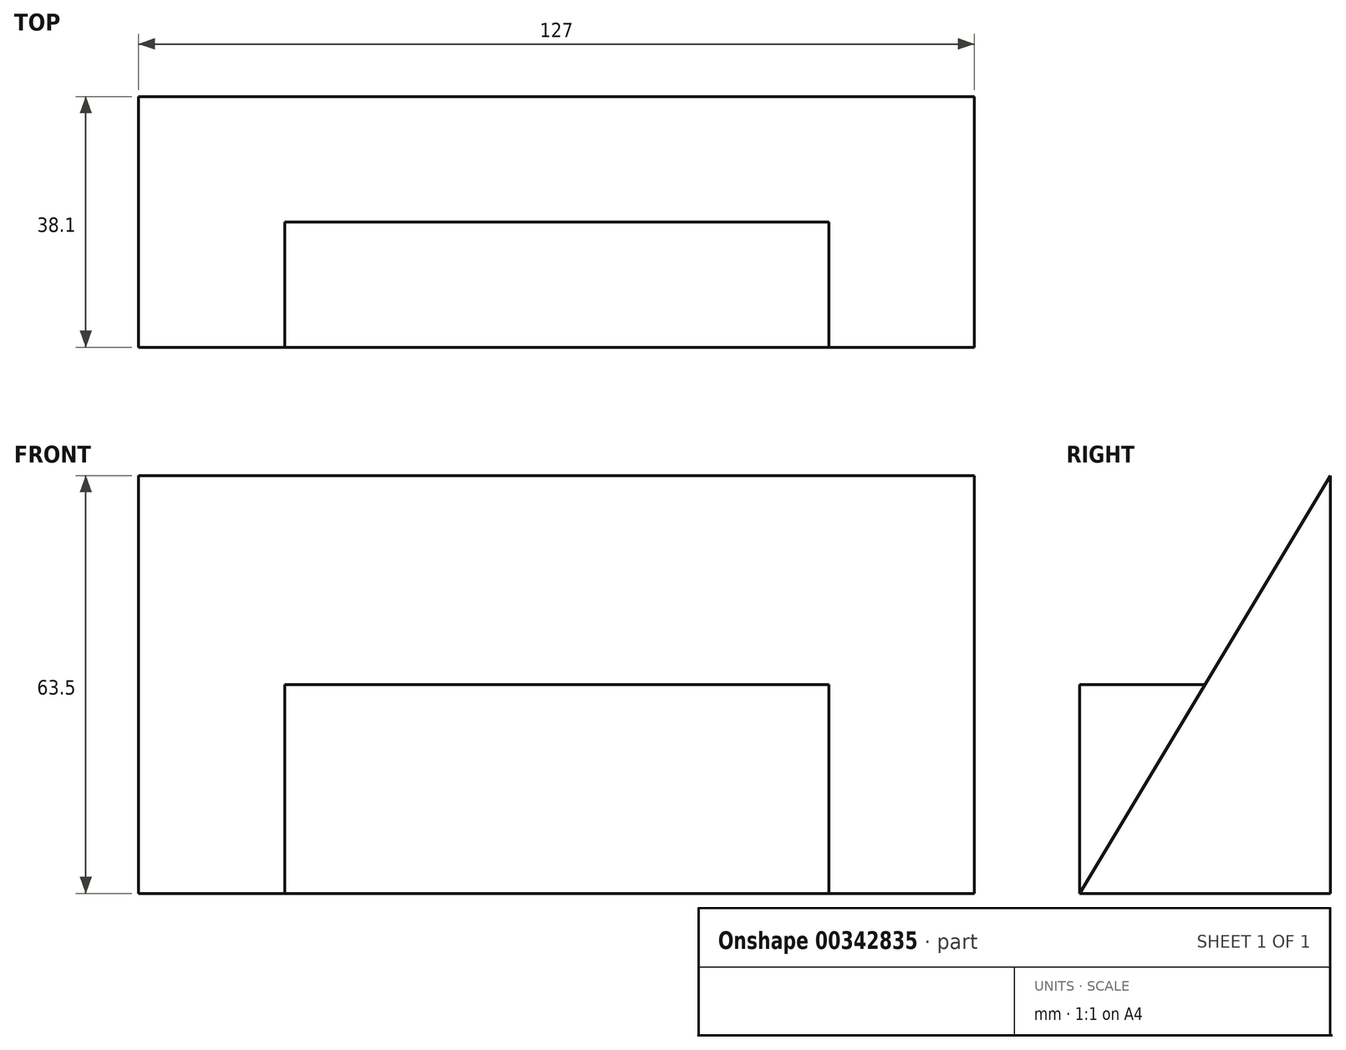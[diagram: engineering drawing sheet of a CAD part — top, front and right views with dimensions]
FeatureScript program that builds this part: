
annotation { "Feature Type Name" : "Feature", "Feature Type Description" : "" }
export const myFeature = defineFeature(function(context is Context, id is Id, definition is map)
    precondition{}
    {
        {
            var Q0;
            Q0=qCreatedBy(makeId("Right.planeOp"),FACE);
            var sketch = newSketch(context, id + "F0", { "sketchPlane" : qUnion([Q0])});
            skLineSegment(sketch, "E0", {"start": v(30.52, 25.08) * mm, "end": v(30.52, -38.42) * mm});
            skLineSegment(sketch, "E1", {"start": v(30.52, -38.42) * mm, "end": v(-7.58, -38.42) * mm});
            skLineSegment(sketch, "E2", {"start": v(-7.58, -38.42) * mm, "end": v(30.52, 25.08) * mm});
            skLineSegment(sketch, "E3", {"start": v(11.77, -6.67) * mm, "end": v(-7.58, -6.67) * mm});
            skLineSegment(sketch, "E4", {"start": v(-7.58, -6.67) * mm, "end": v(-7.58, -38.42) * mm});
            skSolve(sketch);
        }
        {
            var Q0;
            Q0=makeQuery(id+"F0.imprint","IMPRINT",FACE,{"disambiguationData":[TD([[makeQuery(id+"F0.imprint","IMPRINT",EDGE,{"derivedFrom":sQuery(id+"F0.wireOp",EDGE,"E0")}),-1.0]])]});
            extrude(context, id + "F1", {"entities" : qUnion([Q0]), "depth" : 127 * mm});
        }
        {
            var Q0;
            {var subQ0=sQuery(id+"F0.wireOp",EDGE,"E4");Q0=makeQuery(id+"F0.imprint","IMPRINT",FACE,{"disambiguationData":[TD([[makeQuery(id+"F0.imprint","IMPRINT",EDGE,{"derivedFrom":subQ0}),1.0]])]});}
            extrude(context, id + "F2", {"entities" : qUnion([Q0]), "operationType" : NewBodyOperationType.ADD, "depth" : 104.9 * mm, "hasSecondDirection" : true, "secondDirectionOppositeDirection" : false, "secondDirectionDepth" : 22.22 * mm});
        }
    });
